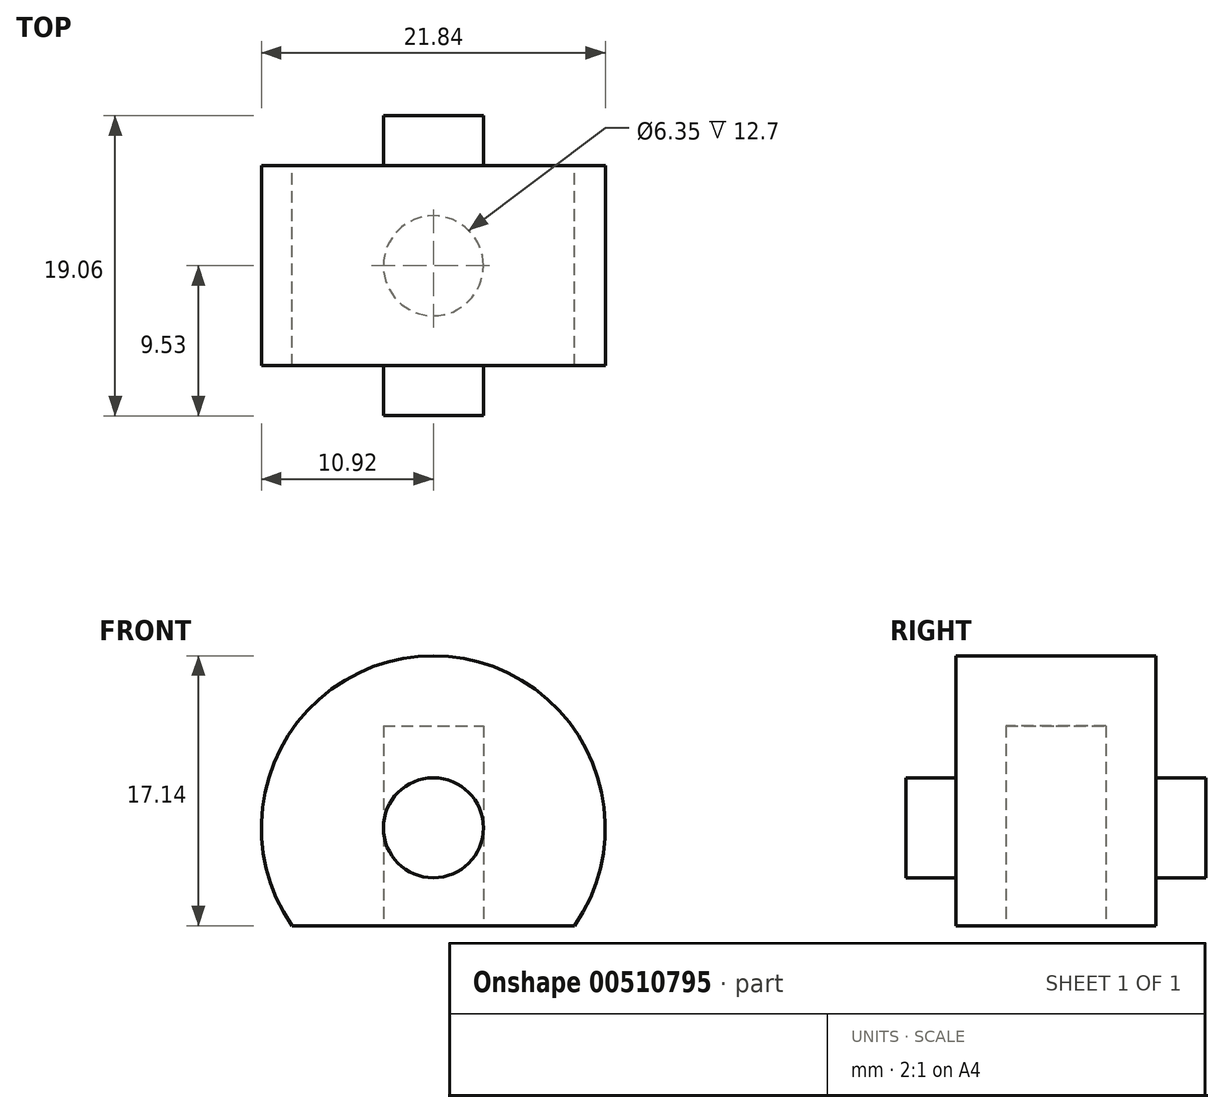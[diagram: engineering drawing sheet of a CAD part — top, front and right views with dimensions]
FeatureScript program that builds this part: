
annotation { "Feature Type Name" : "Feature", "Feature Type Description" : "" }
export const myFeature = defineFeature(function(context is Context, id is Id, definition is map)
    precondition{}
    {
        {
            var Q0;
            Q0=qCreatedBy(makeId("Front.planeOp"),FACE);
            var sketch = newSketch(context, id + "F0", { "sketchPlane" : qUnion([Q0])});
            skCircle(sketch, "E0", {"center": v(0, 0) * mm, "radius": 10.92 * mm});
            skCircle(sketch, "E1", {"center": v(0, 0) * mm, "radius": 3.18 * mm});
            skLineSegment(sketch, "E2", {"start": v(22.38, -6.22) * mm, "end": v(-24, -6.22) * mm});
            skSolve(sketch);
        }
        {
            var Q0;
            Q0=makeQuery(id+"F0.imprint","IMPRINT",FACE,{"disambiguationData":[TD([[makeQuery(id+"F0.imprint","IMPRINT",EDGE,{"derivedFrom":sQuery(id+"F0.wireOp",EDGE,"E1")}),-1.0]])]});
            extrude(context, id + "F1", {"entities" : qUnion([Q0]), "endBound" : BoundingType.SYMMETRIC, "depth" : 12.7 * mm, "offsetDistance" : 25.4 * mm});
        }
        {
            var Q0;
            Q0=makeQuery(id+"F0.imprint","IMPRINT",FACE,{"disambiguationData":[TD([[makeQuery(id+"F0.imprint","IMPRINT",EDGE,{"derivedFrom":sQuery(id+"F0.wireOp",EDGE,"E1")}),1.0]])]});
            extrude(context, id + "F2", {"entities" : qUnion([Q0]), "operationType" : NewBodyOperationType.ADD, "endBound" : BoundingType.SYMMETRIC, "depth" : 19.05 * mm, "offsetDistance" : 25.4 * mm});
        }
        {
            var Q0;
            Q0=makeQuery(id+"F1.opExtrude","SWEPT_FACE",FACE,{"disambiguationData":[OSD([sQuery(id+"F0.wireOp",EDGE,"E2")])]});
            var sketch = newSketch(context, id + "F3", { "sketchPlane" : qUnion([Q0])});
            skCircle(sketch, "E3", {"center": v(0, 0) * mm, "radius": 3.18 * mm});
            skSolve(sketch);
        }
        {
            var Q0;
            Q0 = qSketchRegion(id + "F3", true);
            extrude(context, id + "F4", {"entities" : qUnion([Q0]), "operationType" : NewBodyOperationType.REMOVE, "oppositeDirection" : true, "depth" : 12.7 * mm, "offsetDistance" : 25.4 * mm});
        }
    });
